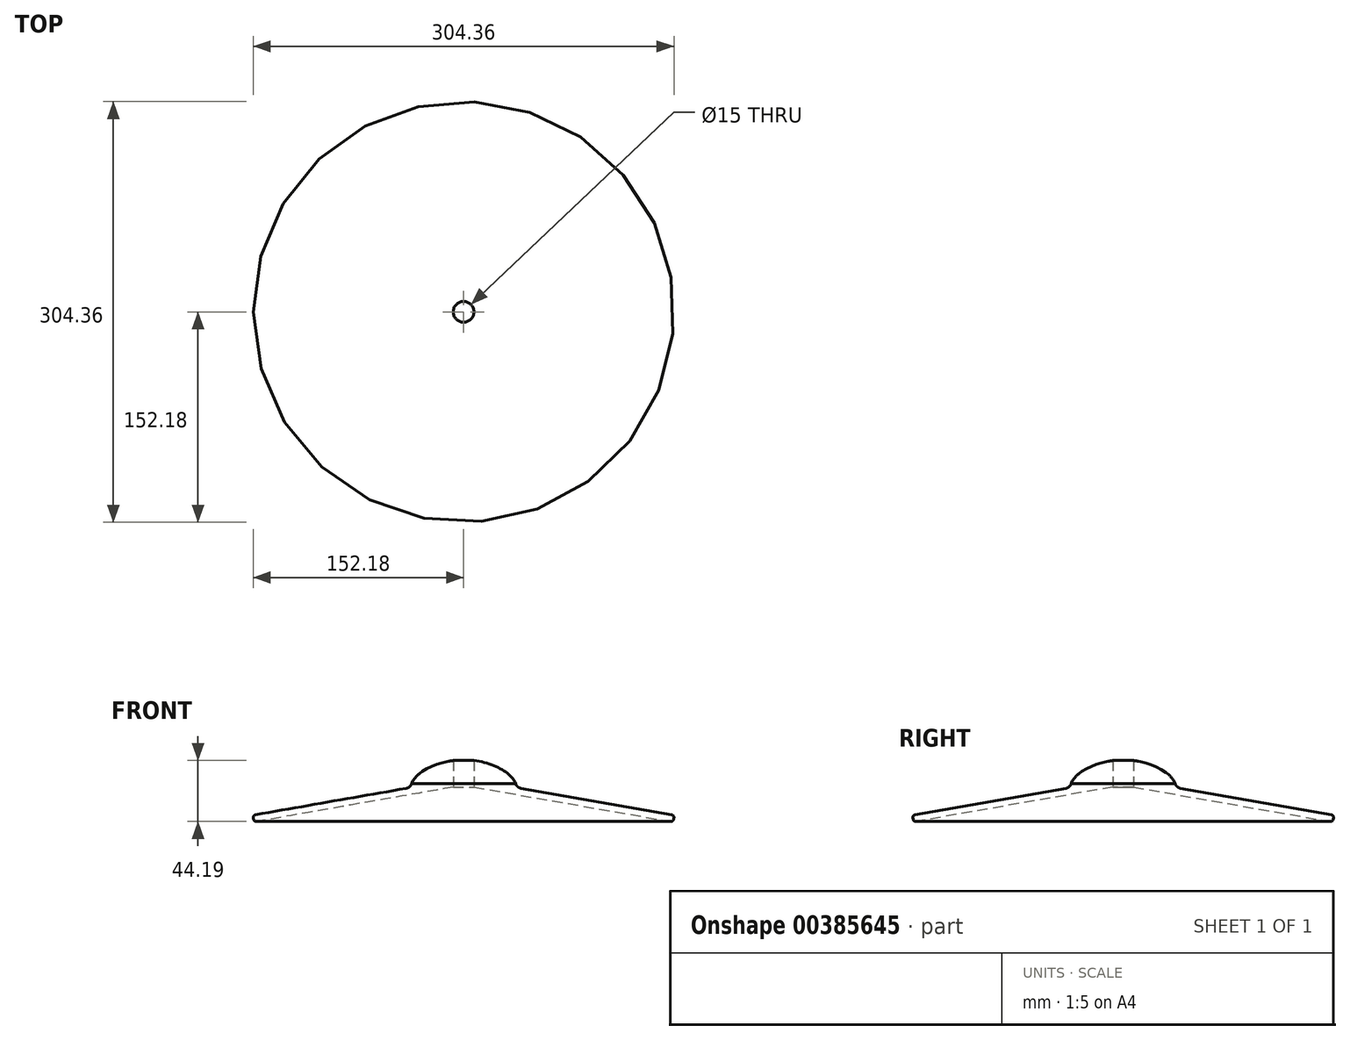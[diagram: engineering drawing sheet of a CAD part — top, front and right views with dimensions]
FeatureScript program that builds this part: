
annotation { "Feature Type Name" : "Feature", "Feature Type Description" : "" }
export const myFeature = defineFeature(function(context is Context, id is Id, definition is map)
    precondition{}
    {
        {
            var Q0;
            Q0=qCreatedBy(makeId("Front.planeOp"),FACE);
            var sketch = newSketch(context, id + "F0", { "sketchPlane" : qUnion([Q0])});
            skLineSegment(sketch, "E0", {"start": v(38.12, 0) * mm, "end": v(152.5, -20.04) * mm});
            skLineSegment(sketch, "E1", {"start": v(152.5, -20.04) * mm, "end": v(151.64, -24.96) * mm});
            skLineSegment(sketch, "E2", {"start": v(151.64, -24.96) * mm, "end": v(0, 1.6) * mm});
            skLineSegment(sketch, "E3", {"start": v(0, 20.04) * mm, "end": v(0, -24.96) * mm, "construction": true});
            skLineSegment(sketch, "E4.bottom", {"start": v(-152.5, 20.04) * mm, "end": v(152.5, 20.04) * mm, "construction": true});
            skLineSegment(sketch, "E4.top", {"start": v(-152.5, -24.96) * mm, "end": v(152.5, -24.96) * mm, "construction": true});
            skLineSegment(sketch, "E4.left", {"start": v(-152.5, 20.04) * mm, "end": v(-152.5, -24.96) * mm, "construction": true});
            skLineSegment(sketch, "E4.right", {"start": v(152.5, 20.04) * mm, "end": v(152.5, -24.96) * mm, "construction": true});
            skLineSegment(sketch, "E5", {"start": v(-38.12, 0) * mm, "end": v(38.12, 0) * mm, "construction": true});
            skLineSegment(sketch, "E6", {"start": v(-38.12, 0) * mm, "end": v(-38.12, 10.02) * mm, "construction": true});
            skLineSegment(sketch, "E7", {"start": v(38.12, 0) * mm, "end": v(38.12, 10.02) * mm, "construction": true});
            skLineSegment(sketch, "E8", {"start": v(-38.12, 10.02) * mm, "end": v(38.12, 10.02) * mm, "construction": true});
            skLineSegment(sketch, "E9", {"start": v(-152.5, -20.04) * mm, "end": v(152.5, -20.04) * mm, "construction": true});
            skLineSegment(sketch, "E10", {"start": v(0, 1.6) * mm, "end": v(0, 20.04) * mm});
            skLineSegment(sketch, "E11", {"start": v(19.06, 20.04) * mm, "end": v(19.06, 0) * mm, "construction": true});
            skFitSpline(sketch, "E12", {"points": [v(0, 20.04) * mm, v(38.12, 0) * mm], "startDerivative": vector(57.19, 0) * mm, "endDerivative": vector(0, -30.06) * mm});
            skSolve(sketch);
        }
        {
            var Q0;
            Q0=qSketchRegion(id+"F0",true);
            var Q1;
            Q1=sQuery(id+"F0.wireOp",EDGE,"E3");
            revolve(context, id + "F1", {"entities" : qUnion([Q0]), "axis" : qUnion([Q1]), "revolveType" : RevolveType.FULL});
        }
        {
            var Q0;
            Q0=qCreatedBy(makeId("Top.planeOp"),FACE);
            var sketch = newSketch(context, id + "F2", { "sketchPlane" : qUnion([Q0])});
            skCircle(sketch, "E13", {"center": v(0, 0) * mm, "radius": 7.5 * mm});
            skSolve(sketch);
        }
        {
            var Q0;
            Q0=qSketchRegion(id+"F2",true);
            extrude(context, id + "F3", {"entities" : qUnion([Q0]), "operationType" : NewBodyOperationType.REMOVE, "endBound" : BoundingType.THROUGH_ALL, "depth" : 25 * mm, "hasSecondDirection" : true, "secondDirectionBound" : SecondDirectionBoundingType.THROUGH_ALL, "secondDirectionOppositeDirection" : true, "secondDirectionDepth" : 25 * mm});
        }
        {
            var Q0;
            Q0=makeQuery(id+"F1.opRevolve","SWEPT_EDGE",EDGE,{"disambiguationData":[OSD([sQuery(id+"F0.wireOp",EDGE,"E1"),sQuery(id+"F0.wireOp",EDGE,"E2")])]});
            var Q1;
            Q1=makeQuery(id+"F1.opRevolve","SWEPT_EDGE",EDGE,{"disambiguationData":[OSD([sQuery(id+"F0.wireOp",EDGE,"E0"),sQuery(id+"F0.wireOp",EDGE,"E1")])]});
            fillet(context, id + "F4", {"entities" : qUnion([Q0, Q1]), "radius" : 2 * mm, "tangentPropagation" : true, "allowEdgeOverflow" : false});
        }
        {
            var Q0;
            Q0=makeQuery(id+"F1.opRevolve","SWEPT_EDGE",EDGE,{"disambiguationData":[OSD([sQuery(id+"F0.wireOp",EDGE,"E0"),sQuery(id+"F0.wireOp",EDGE,"E12")])]});
            fillet(context, id + "F5", {"entities" : qUnion([Q0]), "radius" : 5 * mm, "tangentPropagation" : true, "allowEdgeOverflow" : false});
        }
    });
